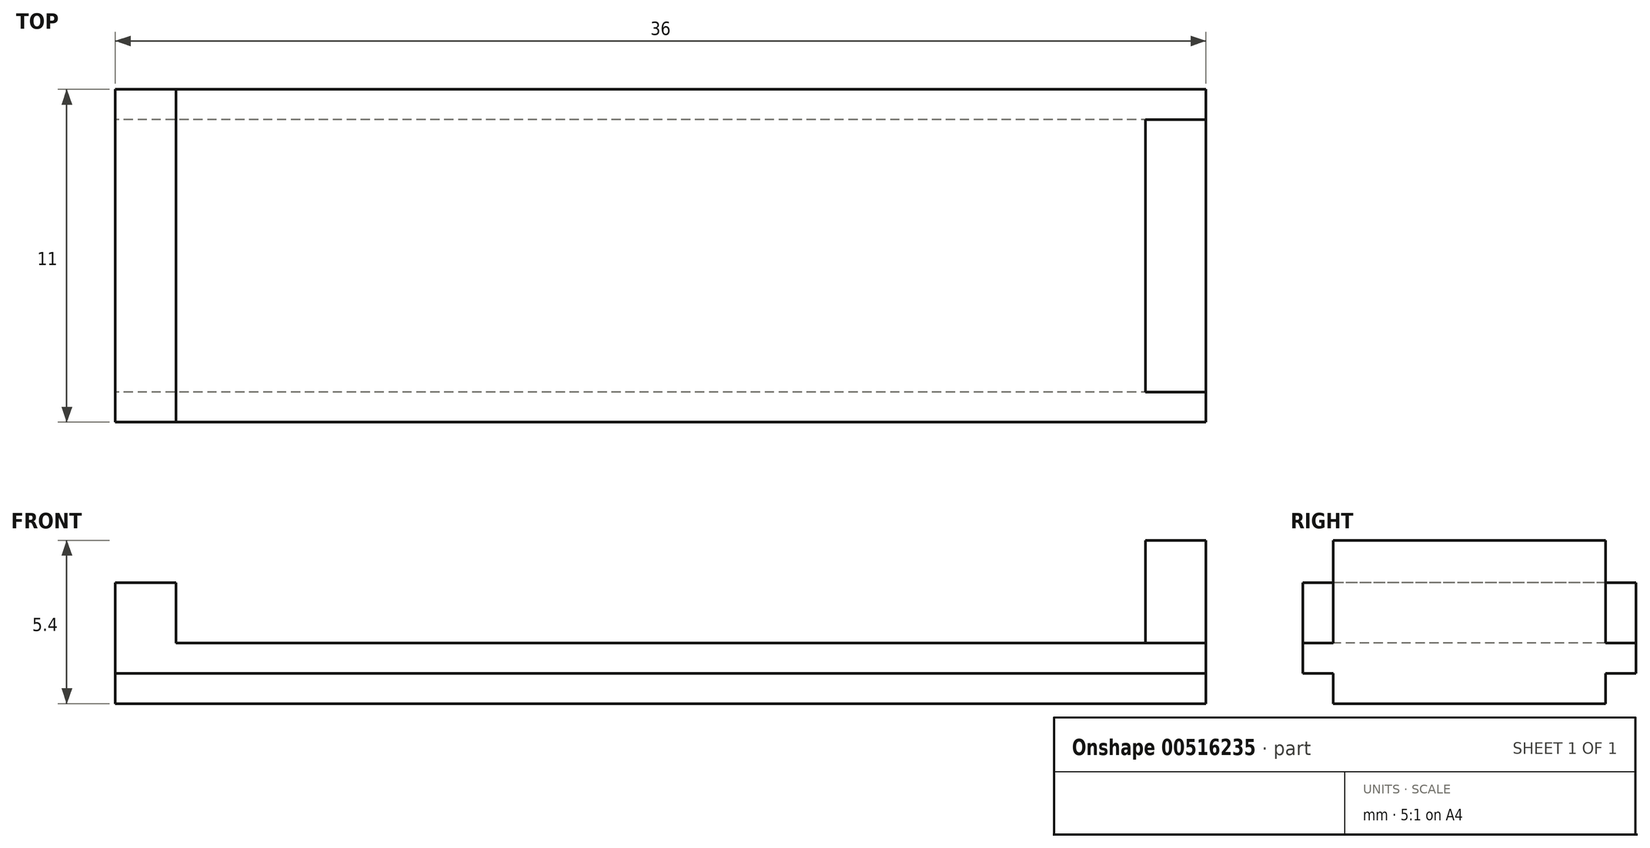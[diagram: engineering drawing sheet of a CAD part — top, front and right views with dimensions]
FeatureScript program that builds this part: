
annotation { "Feature Type Name" : "Feature", "Feature Type Description" : "" }
export const myFeature = defineFeature(function(context is Context, id is Id, definition is map)
    precondition{}
    {
        {
            var Q0;
            Q0=qCreatedBy(makeId("Right.planeOp"),FACE);
            var sketch = newSketch(context, id + "F0", { "sketchPlane" : qUnion([Q0])});
            skLineSegment(sketch, "E0.bottom", {"start": v(4.5, 2) * mm, "end": v(-4.5, 2) * mm});
            skLineSegment(sketch, "E0.top", {"start": v(4.5, 0) * mm, "end": v(-4.5, 0) * mm});
            skLineSegment(sketch, "E0.left", {"start": v(4.5, 2) * mm, "end": v(4.5, 0) * mm});
            skLineSegment(sketch, "E0.right", {"start": v(-4.5, 2) * mm, "end": v(-4.5, 0) * mm});
            skLineSegment(sketch, "E1.bottom", {"start": v(4.5, 2) * mm, "end": v(5.5, 2) * mm});
            skLineSegment(sketch, "E1.top", {"start": v(4.5, 1) * mm, "end": v(5.5, 1) * mm});
            skLineSegment(sketch, "E1.left", {"start": v(4.5, 2) * mm, "end": v(4.5, 1) * mm});
            skLineSegment(sketch, "E1.right", {"start": v(5.5, 2) * mm, "end": v(5.5, 1) * mm});
            skPoint(sketch, "E2.oppositeSnap0", {"position": v(-4.5, 1) * mm});
            skLineSegment(sketch, "E2.bottom", {"start": v(-4.5, 2) * mm, "end": v(-5.5, 2) * mm});
            skLineSegment(sketch, "E2.top", {"start": v(-4.5, 1) * mm, "end": v(-5.5, 1) * mm});
            skLineSegment(sketch, "E2.left", {"start": v(-4.5, 2) * mm, "end": v(-4.5, 1) * mm});
            skLineSegment(sketch, "E2.right", {"start": v(-5.5, 2) * mm, "end": v(-5.5, 1) * mm});
            skSolve(sketch);
        }
        {
            var Q0;
            Q0=makeQuery(id+"F0.imprint","IMPRINT",FACE,{"disambiguationData":[TD([[makeQuery(id+"F0.imprint","IMPRINT",EDGE,{"derivedFrom":sQuery(id+"F0.wireOp",EDGE,"E0.bottom")}),1.0]])]});
            var Q1;
            Q1=makeQuery(id+"F0.imprint","IMPRINT",FACE,{"disambiguationData":[TD([[makeQuery(id+"F0.imprint","IMPRINT",EDGE,{"derivedFrom":sQuery(id+"F0.wireOp",EDGE,"E1.bottom")}),-1.0]])]});
            var Q2;
            Q2=makeQuery(id+"F0.imprint","IMPRINT",FACE,{"disambiguationData":[TD([[makeQuery(id+"F0.imprint","IMPRINT",EDGE,{"derivedFrom":sQuery(id+"F0.wireOp",EDGE,"E2.bottom")}),1.0]])]});
            extrude(context, id + "F1", {"entities" : qUnion([Q0, Q1, Q2]), "depth" : 32 * mm, "offsetDistance" : 25 * mm, "hasSecondDirection" : true, "secondDirectionOppositeDirection" : true, "secondDirectionDepth" : 4 * mm});
        }
        {
            var Q0;
            Q0=makeQuery(id+"F1.opExtrude","SWEPT_FACE",FACE,{"disambiguationData":[OSD([sQuery(id+"F0.wireOp",EDGE,"E0.bottom"),sQuery(id+"F0.wireOp",EDGE,"E1.bottom"),sQuery(id+"F0.wireOp",EDGE,"E2.bottom")])]});
            var sketch = newSketch(context, id + "F2", { "sketchPlane" : qUnion([Q0])});
            skLineSegment(sketch, "E3.bottom", {"start": v(30, 4.5) * mm, "end": v(32, 4.5) * mm});
            skLineSegment(sketch, "E3.top", {"start": v(30, -4.5) * mm, "end": v(32, -4.5) * mm});
            skLineSegment(sketch, "E3.left", {"start": v(30, 4.5) * mm, "end": v(30, -4.5) * mm});
            skLineSegment(sketch, "E3.right", {"start": v(32, 4.5) * mm, "end": v(32, -4.5) * mm});
            skSolve(sketch);
        }
        {
            var Q0;
            Q0=makeQuery(id+"F2.imprint","IMPRINT",FACE,{"disambiguationData":[TD([[makeQuery(id+"F2.imprint","IMPRINT",EDGE,{"derivedFrom":sQuery(id+"F2.wireOp",EDGE,"E3.bottom")}),-1.0]])]});
            extrude(context, id + "F3", {"entities" : qUnion([Q0]), "depth" : (5.4 - 2) * mm, "offsetDistance" : 25 * mm});
        }
        {
            var Q0;
            Q0=makeQuery(id+"F1.opExtrude","CAP_FACE",FACE,{"disambiguationData":[OSD([sQuery(id+"F0.wireOp",EDGE,"E0.bottom"),sQuery(id+"F0.wireOp",EDGE,"E0.top"),sQuery(id+"F0.wireOp",EDGE,"E0.left"),sQuery(id+"F0.wireOp",EDGE,"E0.right"),sQuery(id+"F0.wireOp",EDGE,"E1.bottom"),sQuery(id+"F0.wireOp",EDGE,"E1.top"),sQuery(id+"F0.wireOp",EDGE,"E1.right"),sQuery(id+"F0.wireOp",EDGE,"E2.bottom"),sQuery(id+"F0.wireOp",EDGE,"E2.top"),sQuery(id+"F0.wireOp",EDGE,"E2.right")])],"isStart":false});
            var sketch = newSketch(context, id + "F4", { "sketchPlane" : qUnion([Q0])});
            skLineSegment(sketch, "E4", {"start": v(-0.38, 2) * mm, "end": v(-0.38, 1.75) * mm});
            skLineSegment(sketch, "E5", {"start": v(-0.38, 1.75) * mm, "end": v(-0.75, 1.75) * mm});
            skLineSegment(sketch, "E6", {"start": v(-0.75, 1.75) * mm, "end": v(-0.75, 1.5) * mm});
            skLineSegment(sketch, "E7", {"start": v(-0.75, 1.5) * mm, "end": v(0.75, 1.5) * mm});
            skLineSegment(sketch, "E8", {"start": v(0.75, 1.5) * mm, "end": v(0.75, 1.75) * mm});
            skLineSegment(sketch, "E9", {"start": v(0.75, 1.75) * mm, "end": v(0.38, 1.75) * mm});
            skLineSegment(sketch, "E10", {"start": v(0.38, 2) * mm, "end": v(-0.38, 2) * mm});
            skLineSegment(sketch, "E11", {"start": v(0.38, 1.75) * mm, "end": v(0.38, 2) * mm});
            skLineSegment(sketch, "E12", {"start": v(0, 0.99) * mm, "end": v(0, 2.67) * mm, "construction": true});
            skPoint(sketch, "E12.endSnap0", {"position": v(0, 2) * mm});
            skSolve(sketch);
        }
        {
            var Q0;
            Q0=makeQuery(id+"F4.imprint","IMPRINT",FACE,{"disambiguationData":[TD([[makeQuery(id+"F4.imprint","IMPRINT",EDGE,{"derivedFrom":sQuery(id+"F4.wireOp",EDGE,"E4")}),1.0]])]});
            extrude(context, id + "F5", {"entities" : qUnion([Q0]), "operationType" : NewBodyOperationType.REMOVE, "oppositeDirection" : true, "depth" : 1 * mm, "offsetDistance" : 25 * mm});
        }
        {
            var Q0;
            Q0=makeQuery(id+"F4.imprint","IMPRINT",FACE,{"disambiguationData":[TD([[makeQuery(id+"F4.imprint","IMPRINT",EDGE,{"derivedFrom":sQuery(id+"F4.wireOp",EDGE,"E4")}),1.0]])]});
            extrude(context, id + "F6", {"entities" : qUnion([Q0]), "operationType" : NewBodyOperationType.ADD, "oppositeDirection" : true, "depth" : 1 * mm, "offsetDistance" : 25 * mm});
        }
        {
            var Q0;
            Q0=makeQuery(id+"F1.opExtrude","SWEPT_FACE",FACE,{"disambiguationData":[OSD([sQuery(id+"F0.wireOp",EDGE,"E0.bottom"),sQuery(id+"F0.wireOp",EDGE,"E1.bottom"),sQuery(id+"F0.wireOp",EDGE,"E2.bottom")])]});
            var sketch = newSketch(context, id + "F7", { "sketchPlane" : qUnion([Q0])});
            skLineSegment(sketch, "E13.bottom", {"start": v(-4, 5.5) * mm, "end": v(-2, 5.5) * mm});
            skLineSegment(sketch, "E13.top", {"start": v(-4, -5.5) * mm, "end": v(-2, -5.5) * mm});
            skLineSegment(sketch, "E13.left", {"start": v(-4, 5.5) * mm, "end": v(-4, -5.5) * mm});
            skLineSegment(sketch, "E13.right", {"start": v(-2, 5.5) * mm, "end": v(-2, -5.5) * mm});
            skSolve(sketch);
        }
        {
            var Q0;
            Q0=makeQuery(id+"F7.imprint","IMPRINT",FACE,{"disambiguationData":[TD([[makeQuery(id+"F7.imprint","IMPRINT",EDGE,{"derivedFrom":sQuery(id+"F7.wireOp",EDGE,"E13.bottom")}),1.0]])]});
            extrude(context, id + "F8", {"entities" : qUnion([Q0]), "operationType" : NewBodyOperationType.ADD, "depth" : 2 * mm, "offsetDistance" : 25 * mm});
        }
    });
